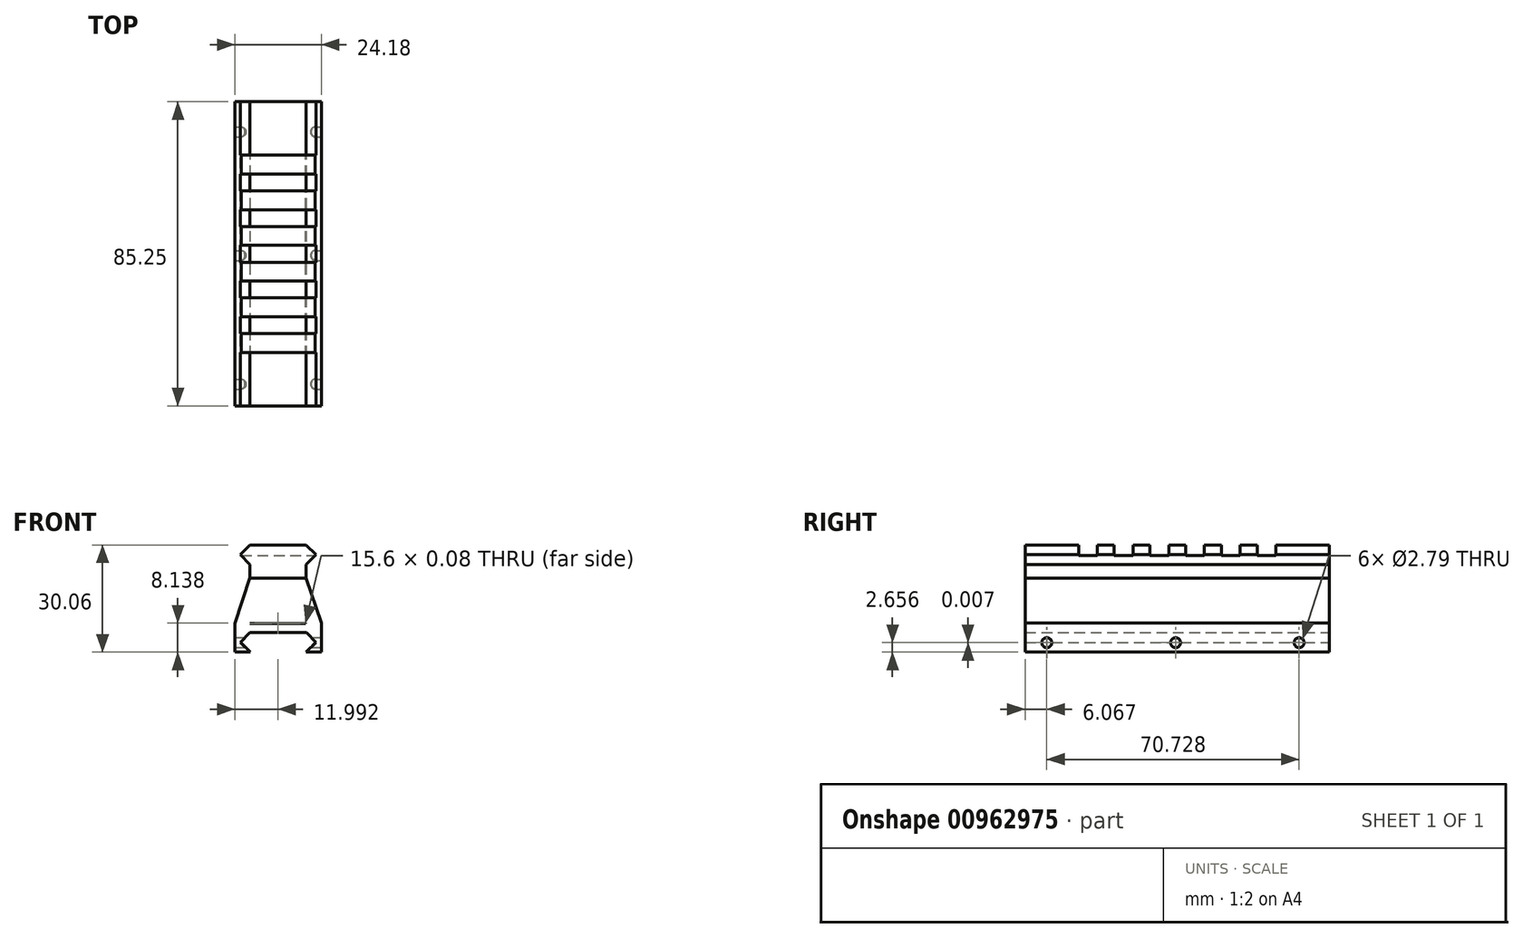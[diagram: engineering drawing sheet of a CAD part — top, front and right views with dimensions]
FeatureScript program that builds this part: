
annotation { "Feature Type Name" : "Feature", "Feature Type Description" : "" }
export const myFeature = defineFeature(function(context is Context, id is Id, definition is map)
    precondition{}
    {
        {
            var Q0;
            Q0=qCreatedBy(makeId("Front.planeOp"),FACE);
            var sketch = newSketch(context, id + "F0", { "sketchPlane" : qUnion([Q0])});
            skLineSegment(sketch, "E0", {"start": v(0, 0) * mm, "end": v(15.67, 0) * mm});
            skPoint(sketch, "E1", {"position": v(0, 9.32) * mm});
            skLineSegment(sketch, "E2", {"start": v(0, 9.32) * mm, "end": v(-2.77, 6.55) * mm});
            skLineSegment(sketch, "E3", {"start": v(0, 9.32) * mm, "end": v(15.67, 9.32) * mm});
            skLineSegment(sketch, "E4", {"start": v(-2.77, 6.56) * mm, "end": v(0, 3.8) * mm});
            skLineSegment(sketch, "E5", {"start": v(0, 3.8) * mm, "end": v(0, 0) * mm});
            skLineSegment(sketch, "E6", {"start": v(15.67, 9.32) * mm, "end": v(18.43, 6.56) * mm});
            skLineSegment(sketch, "E7", {"start": v(18.43, 6.56) * mm, "end": v(15.67, 3.8) * mm});
            skLineSegment(sketch, "E8", {"start": v(15.67, 3.8) * mm, "end": v(15.67, 0) * mm});
            skSolve(sketch);
        }
        {
            var Q0;
            Q0=makeQuery(id+"F0.imprint","IMPRINT",FACE,{"disambiguationData":[TD([[makeQuery(id+"F0.imprint","IMPRINT",EDGE,{"derivedFrom":sQuery(id+"F0.wireOp",EDGE,"E0")}),1.0]])]});
            extrude(context, id + "F1", {"entities" : qUnion([Q0]), "depth" : 85.25 * mm, "offsetDistance" : 25 * mm});
        }
        {
            var Q0;
            Q0=makeQuery(id+"F1.opExtrude","SWEPT_FACE",FACE,{"disambiguationData":[OSD([sQuery(id+"F0.wireOp",EDGE,"E3")])]});
            var sketch = newSketch(context, id + "F2", { "sketchPlane" : qUnion([Q0])});
            skLineSegment(sketch, "E9", {"start": v(-19.7, -15) * mm, "end": v(36.12, -15) * mm});
            skLineSegment(sketch, "E10", {"start": v(-19.7, -20.25) * mm, "end": v(36.12, -20.25) * mm});
            skLineSegment(sketch, "E11", {"start": v(-19.7, -15) * mm, "end": v(-19.7, -20.25) * mm});
            skLineSegment(sketch, "E12", {"start": v(36.12, -15) * mm, "end": v(36.12, -20.25) * mm});
            skPoint(sketch, "E13", {"position": v(-19.7, -25) * mm});
            skLineSegment(sketch, "E14.0.1.0", {"start": v(-19.7, -25) * mm, "end": v(36.12, -25) * mm});
            skLineSegment(sketch, "E14.0.1.1", {"start": v(-19.7, -25) * mm, "end": v(-19.7, -30.25) * mm});
            skPoint(sketch, "E14.0.1.2", {"position": v(-19.7, -35) * mm});
            skLineSegment(sketch, "E14.0.1.3", {"start": v(-19.7, -30.25) * mm, "end": v(36.12, -30.25) * mm});
            skLineSegment(sketch, "E14.0.1.4", {"start": v(36.12, -25) * mm, "end": v(36.12, -30.25) * mm});
            skLineSegment(sketch, "E14.0.2.0", {"start": v(-19.7, -35) * mm, "end": v(36.12, -35) * mm});
            skLineSegment(sketch, "E14.0.2.1", {"start": v(-19.7, -35) * mm, "end": v(-19.7, -40.25) * mm});
            skPoint(sketch, "E14.0.2.2", {"position": v(-19.7, -45) * mm});
            skLineSegment(sketch, "E14.0.2.3", {"start": v(-19.7, -40.25) * mm, "end": v(36.12, -40.25) * mm});
            skLineSegment(sketch, "E14.0.2.4", {"start": v(36.12, -35) * mm, "end": v(36.12, -40.25) * mm});
            skLineSegment(sketch, "E14.0.3.0", {"start": v(-19.7, -45) * mm, "end": v(36.12, -45) * mm});
            skLineSegment(sketch, "E14.0.3.1", {"start": v(-19.7, -45) * mm, "end": v(-19.7, -50.25) * mm});
            skPoint(sketch, "E14.0.3.2", {"position": v(-19.7, -55) * mm});
            skLineSegment(sketch, "E14.0.3.3", {"start": v(-19.7, -50.25) * mm, "end": v(36.12, -50.25) * mm});
            skLineSegment(sketch, "E14.0.3.4", {"start": v(36.12, -45) * mm, "end": v(36.12, -50.25) * mm});
            skLineSegment(sketch, "E14.0.4.0", {"start": v(-19.7, -55) * mm, "end": v(36.12, -55) * mm});
            skLineSegment(sketch, "E14.0.4.1", {"start": v(-19.7, -55) * mm, "end": v(-19.7, -60.25) * mm});
            skPoint(sketch, "E14.0.4.2", {"position": v(-19.7, -65) * mm});
            skLineSegment(sketch, "E14.0.4.3", {"start": v(-19.7, -60.25) * mm, "end": v(36.12, -60.25) * mm});
            skLineSegment(sketch, "E14.0.4.4", {"start": v(36.12, -55) * mm, "end": v(36.12, -60.25) * mm});
            skLineSegment(sketch, "E14.0.5.0", {"start": v(-19.7, -65) * mm, "end": v(36.12, -65) * mm});
            skLineSegment(sketch, "E14.0.5.1", {"start": v(-19.7, -65) * mm, "end": v(-19.7, -70.25) * mm});
            skPoint(sketch, "E14.0.5.2", {"position": v(-19.7, -75) * mm});
            skLineSegment(sketch, "E14.0.5.3", {"start": v(-19.7, -70.25) * mm, "end": v(36.12, -70.25) * mm});
            skLineSegment(sketch, "E14.0.5.4", {"start": v(36.12, -65) * mm, "end": v(36.12, -70.25) * mm});
            skLineSegment(sketch, "E14.direction1", {"start": v(-19.7, -15) * mm, "end": v(12.9, -15) * mm, "construction": true});
            skLineSegment(sketch, "E14.direction2", {"start": v(-19.7, -15) * mm, "end": v(-19.7, -25) * mm, "construction": true});
            skSolve(sketch);
        }
        {
            var Q0;
            Q0=qSketchRegion(id+"F2",true);
            extrude(context, id + "F3", {"entities" : qUnion([Q0]), "operationType" : NewBodyOperationType.REMOVE, "oppositeDirection" : true, "depth" : 3 * mm, "offsetDistance" : 25 * mm});
        }
        {
            var Q0;
            Q0=qCreatedBy(makeId("Front.planeOp"),FACE);
            var sketch = newSketch(context, id + "F4", { "sketchPlane" : qUnion([Q0])});
            skLineSegment(sketch, "E15.top", {"start": v(0, -2.55) * mm, "end": v(0, -2.55) * mm});
            skLineSegment(sketch, "E16", {"start": v(15.68, -20.74) * mm, "end": v(18.45, -17.97) * mm});
            skLineSegment(sketch, "E17", {"start": v(18.45, -17.97) * mm, "end": v(15.68, -15.21) * mm});
            skLineSegment(sketch, "E18.MirrorCS", {"start": v(-2.69, -17.97) * mm, "end": v(0.09, -15.2) * mm});
            skLineSegment(sketch, "E19.MirrorCS", {"start": v(0.08, -20.74) * mm, "end": v(-2.69, -17.97) * mm});
            skLineSegment(sketch, "E20.bottom", {"start": v(0.08, -20.74) * mm, "end": v(-4.19, -20.74) * mm});
            skLineSegment(sketch, "E21.top", {"start": v(15.76, -15.3) * mm, "end": v(0, -15.3) * mm});
            skLineSegment(sketch, "E22.right", {"start": v(-4.19, -12.66) * mm, "end": v(-4.19, -20.74) * mm});
            skLineSegment(sketch, "E23.top", {"start": v(20, -20.74) * mm, "end": v(15.68, -20.74) * mm});
            skLineSegment(sketch, "E23.left", {"start": v(20, -12.54) * mm, "end": v(20, -20.74) * mm});
            skLineSegment(sketch, "E23.right", {"start": v(15.6, 0.12) * mm, "end": v(15.6, 0) * mm});
            skLineSegment(sketch, "E24", {"start": v(20, -12.54) * mm, "end": v(-4.19, -12.66) * mm});
            skLineSegment(sketch, "E25.bottom", {"start": v(15.6, 0.12) * mm, "end": v(0, 0.12) * mm});
            skLineSegment(sketch, "E25.top", {"start": v(15.6, -12.64) * mm, "end": v(0, -12.64) * mm});
            skLineSegment(sketch, "E25.left", {"start": v(15.6, 0.12) * mm, "end": v(15.6, -12.64) * mm});
            skLineSegment(sketch, "E25.right", {"start": v(0, 0.12) * mm, "end": v(0, -12.64) * mm});
            skLineSegment(sketch, "E26", {"start": v(15.6, 0.12) * mm, "end": v(20, -12.54) * mm});
            skLineSegment(sketch, "E27", {"start": v(0, 0.12) * mm, "end": v(-4.19, -12.66) * mm});
            skSolve(sketch);
        }
        {
            var Q0;
            {var subQ2=sQuery(id+"F4.wireOp",EDGE,"E25.bottom");Q0=makeQuery(id+"F4.imprint","IMPRINT",FACE,{"disambiguationData":[TD([[makeQuery(id+"F4.imprint","IMPRINT",EDGE,{"derivedFrom":subQ2}),1.0]])]});}
            var Q1;
            {var subQ6=sQuery(id+"F4.wireOp",EDGE,"E16");Q1=makeQuery(id+"F4.imprint","IMPRINT",FACE,{"disambiguationData":[TD([[makeQuery(id+"F4.imprint","IMPRINT",EDGE,{"derivedFrom":subQ6}),-1.0]])]});}
            var Q2;
            {var subQ0=sQuery(id+"F4.wireOp",EDGE,"E26");Q2=makeQuery(id+"F4.imprint","IMPRINT",FACE,{"disambiguationData":[TD([[makeQuery(id+"F4.imprint","IMPRINT",EDGE,{"derivedFrom":subQ0}),-1.0]])]});}
            var Q3;
            {var subQ0=sQuery(id+"F4.wireOp",EDGE,"E27");Q3=makeQuery(id+"F4.imprint","IMPRINT",FACE,{"disambiguationData":[TD([[makeQuery(id+"F4.imprint","IMPRINT",EDGE,{"derivedFrom":subQ0}),1.0]])]});}
            extrude(context, id + "F5", {"entities" : qUnion([Q0, Q1, Q2, Q3]), "operationType" : NewBodyOperationType.ADD, "depth" : 85.24 * mm, "offsetDistance" : 25.4 * mm});
        }
        {
            var Q0;
            Q0=qCreatedBy(makeId("Right.planeOp"),FACE);
            var sketch = newSketch(context, id + "F6", { "sketchPlane" : qUnion([Q0])});
            skPoint(sketch, "E28", {"position": v(-8.46, -18.08) * mm});
            skPoint(sketch, "E29", {"position": v(-79.18, -18.08) * mm});
            skPoint(sketch, "E30", {"position": v(-43.07, -18.08) * mm});
            skSolve(sketch);
        }
        {
            var Q0;
            Q0=makeQuery(id+"F5.opExtrude","SWEPT_FACE",FACE,{"disambiguationData":[OSD([sQuery(id+"F4.wireOp",EDGE,"E23.left")])]});
            var sketch = newSketch(context, id + "F7", { "sketchPlane" : qUnion([Q0])});
            skPoint(sketch, "E31", {"position": v(-79.18, -18.08) * mm});
            skPoint(sketch, "E32", {"position": v(-43.08, -18.08) * mm});
            skPoint(sketch, "E33", {"position": v(-8.45, -18.08) * mm});
            skSolve(sketch);
        }
        {
            var Q0;
            Q0=sQuery(id+"F6.wireOp",VERTEX,"E29");
            var Q1;
            Q1=sQuery(id+"F6.wireOp",VERTEX,"E30");
            var Q2;
            Q2=sQuery(id+"F6.wireOp",VERTEX,"E28");
            var Q3;
            Q3=sQuery(id+"F7.wireOp",VERTEX,"E31");
            var Q4;
            Q4=sQuery(id+"F7.wireOp",VERTEX,"E32");
            var Q5;
            Q5=sQuery(id+"F7.wireOp",VERTEX,"E33");
            var Q6;
            Q6=makeQuery(id+"F5.opExtrude","SWEPT_BODY",BODY,{"disambiguationData":[OSD([sQuery(id+"F4.wireOp",EDGE,"E16"),sQuery(id+"F4.wireOp",EDGE,"E17"),sQuery(id+"F4.wireOp",EDGE,"E18.MirrorCS"),sQuery(id+"F4.wireOp",EDGE,"E19.MirrorCS"),sQuery(id+"F4.wireOp",EDGE,"E20.bottom"),sQuery(id+"F4.wireOp",EDGE,"E21.top"),sQuery(id+"F4.wireOp",EDGE,"E22.right"),sQuery(id+"F4.wireOp",EDGE,"E23.top"),sQuery(id+"F4.wireOp",EDGE,"E23.left"),sQuery(id+"F4.wireOp",EDGE,"E24"),sQuery(id+"F4.wireOp",EDGE,"E25.top"),sQuery(id+"F4.wireOp",EDGE,"E25.left"),sQuery(id+"F4.wireOp",EDGE,"E25.right")])]});
            var Q7;
            Q7=makeQuery(id+"F1.opExtrude","SWEPT_BODY",BODY,{"disambiguationData":[OSD([sQuery(id+"F0.wireOp",EDGE,"E0"),sQuery(id+"F0.wireOp",EDGE,"E2"),sQuery(id+"F0.wireOp",EDGE,"E3"),sQuery(id+"F0.wireOp",EDGE,"E4"),sQuery(id+"F0.wireOp",EDGE,"E5"),sQuery(id+"F0.wireOp",EDGE,"E6"),sQuery(id+"F0.wireOp",EDGE,"E7"),sQuery(id+"F0.wireOp",EDGE,"E8")])]});
            hole(context, id + "F8", {"style" : HoleStyle.SIMPLE, "endStyle" : HoleEndStyle.BLIND, "holeDiameter" : 2.8 * mm, "majorDiameter" : 6.35 * mm, "holeDepth" : 12.7 * mm, "isTappedThrough" : true, "tappedDepth" : 12.7 * mm, "tapClearance" : 3, "locations" : qUnion([Q0, Q1, Q2, Q3, Q4, Q5]), "scope" : qUnion([Q6, Q7])});
        }
    });
